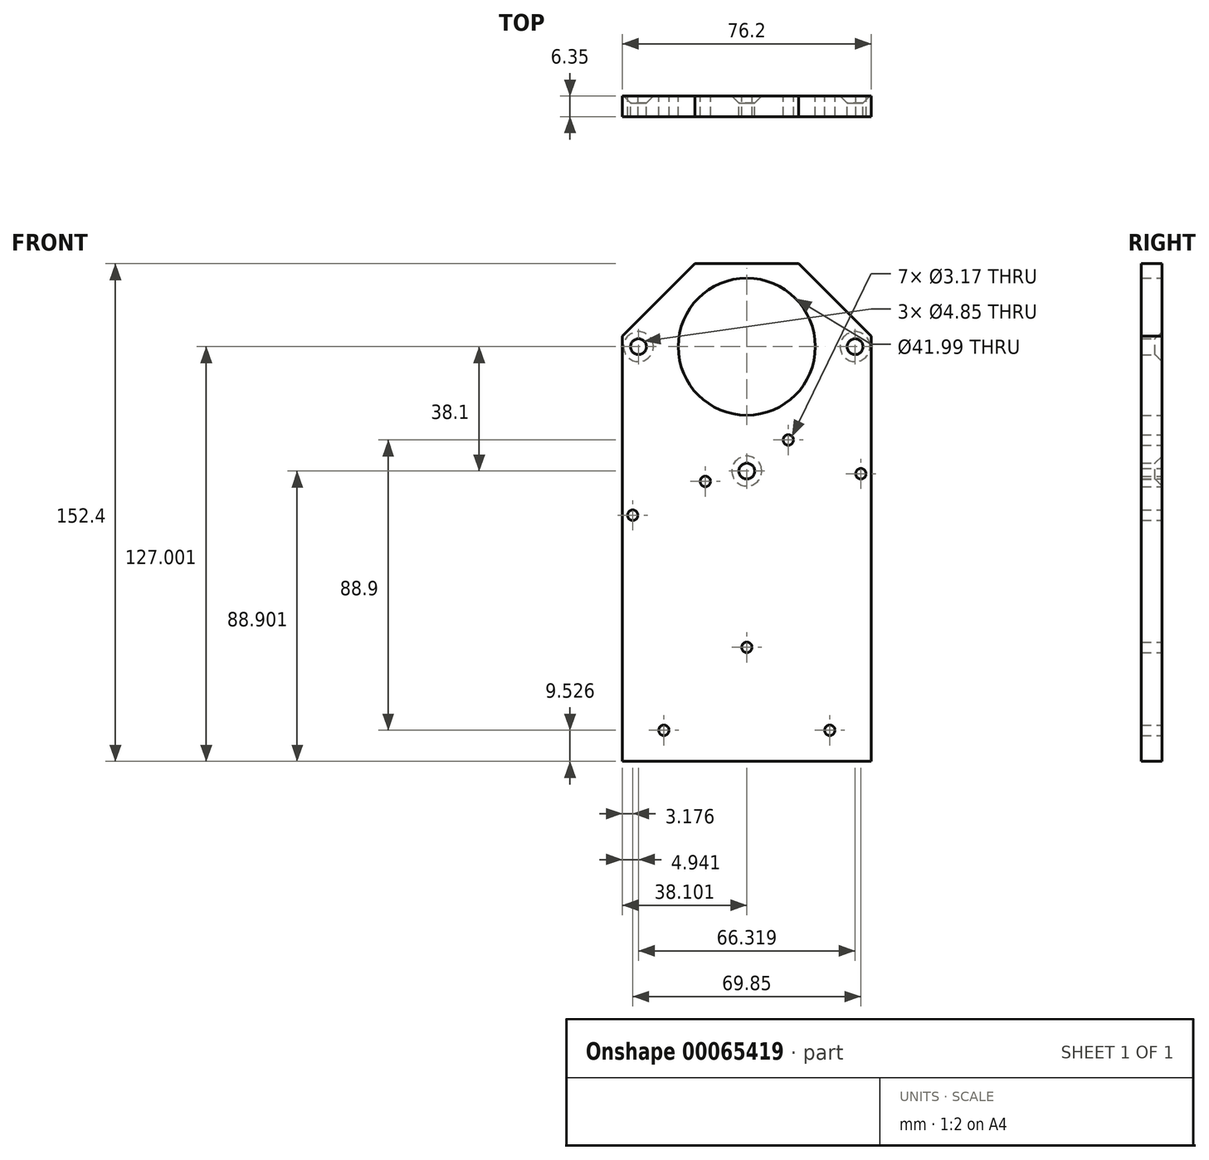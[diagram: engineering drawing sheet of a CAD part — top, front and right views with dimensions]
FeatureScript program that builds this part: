
annotation { "Feature Type Name" : "Feature", "Feature Type Description" : "" }
export const myFeature = defineFeature(function(context is Context, id is Id, definition is map)
    precondition{}
    {
        {
            var Q0;
            Q0=qCreatedBy(makeId("Front.planeOp"),FACE);
            var sketch = newSketch(context, id + "F0", { "sketchPlane" : qUnion([Q0])});
            skLineSegment(sketch, "E0", {"start": v(-20.16, 46.71) * mm, "end": v(11.59, 46.71) * mm});
            skLineSegment(sketch, "E1", {"start": v(11.59, 46.71) * mm, "end": v(33.81, 24.49) * mm});
            skLineSegment(sketch, "E2", {"start": v(-20.16, 46.71) * mm, "end": v(-42.39, 24.49) * mm});
            skLineSegment(sketch, "E3", {"start": v(-42.39, 24.49) * mm, "end": v(-42.39, -105.69) * mm});
            skLineSegment(sketch, "E4", {"start": v(33.81, 24.49) * mm, "end": v(33.81, -105.69) * mm});
            skLineSegment(sketch, "E5", {"start": v(33.81, -105.69) * mm, "end": v(-42.39, -105.69) * mm});
            skLineSegment(sketch, "E6", {"start": v(33.81, 24.49) * mm, "end": v(33.81, 21.31) * mm});
            skLineSegment(sketch, "E7", {"start": v(33.81, 21.31) * mm, "end": v(28.87, 21.31) * mm});
            skCircle(sketch, "E8", {"center": v(28.87, 21.31) * mm, "radius": 2.43 * mm});
            skLineSegment(sketch, "E9", {"start": v(-4.29, 46.71) * mm, "end": v(-4.29, -105.69) * mm});
            skLineSegment(sketch, "E10", {"start": v(33.81, 21.31) * mm, "end": v(33.81, -7.26) * mm});
            skLineSegment(sketch, "E11", {"start": v(33.81, -7.26) * mm, "end": v(8.41, -7.26) * mm});
            skLineSegment(sketch, "E12", {"start": v(33.81, -7.26) * mm, "end": v(33.81, -17.58) * mm});
            skLineSegment(sketch, "E13", {"start": v(33.81, -17.58) * mm, "end": v(30.64, -17.58) * mm});
            skLineSegment(sketch, "E14", {"start": v(-42.39, 24.49) * mm, "end": v(-42.39, -19.96) * mm});
            skLineSegment(sketch, "E15", {"start": v(-42.39, -19.96) * mm, "end": v(-16.99, -19.96) * mm});
            skLineSegment(sketch, "E16", {"start": v(-42.39, -19.96) * mm, "end": v(-42.39, -30.28) * mm});
            skLineSegment(sketch, "E17", {"start": v(-42.39, -30.28) * mm, "end": v(-39.21, -30.28) * mm});
            skCircle(sketch, "E18", {"center": v(-16.99, -19.96) * mm, "radius": 1.59 * mm});
            skCircle(sketch, "E19", {"center": v(-39.21, -30.28) * mm, "radius": 1.59 * mm});
            skCircle(sketch, "E20", {"center": v(8.41, -7.26) * mm, "radius": 1.59 * mm});
            skLineSegment(sketch, "E21", {"start": v(-16.99, -19.96) * mm, "end": v(-4.29, -19.96) * mm});
            skLineSegment(sketch, "E22", {"start": v(-4.29, -19.96) * mm, "end": v(-4.29, -16.79) * mm});
            skCircle(sketch, "E23", {"center": v(-4.29, -16.79) * mm, "radius": 2.43 * mm});
            skLineSegment(sketch, "E24", {"start": v(28.87, 21.31) * mm, "end": v(-4.29, 21.31) * mm});
            skCircle(sketch, "E25", {"center": v(-4.29, 21.31) * mm, "radius": 21 * mm});
            skLineSegment(sketch, "E26", {"start": v(-4.29, -105.69) * mm, "end": v(-4.29, -70.76) * mm});
            skLineSegment(sketch, "E27", {"start": v(-42.39, -105.69) * mm, "end": v(-29.69, -105.69) * mm});
            skLineSegment(sketch, "E28", {"start": v(33.81, -105.69) * mm, "end": v(21.11, -105.69) * mm});
            skLineSegment(sketch, "E29", {"start": v(21.11, -105.69) * mm, "end": v(21.11, -96.16) * mm});
            skLineSegment(sketch, "E30", {"start": v(-29.69, -105.69) * mm, "end": v(-29.69, -96.16) * mm});
            skCircle(sketch, "E31", {"center": v(-29.69, -96.16) * mm, "radius": 1.59 * mm});
            skCircle(sketch, "E32", {"center": v(21.11, -96.16) * mm, "radius": 1.59 * mm});
            skCircle(sketch, "E33", {"center": v(-4.29, -70.76) * mm, "radius": 1.59 * mm});
            skCircle(sketch, "E34.MirrorC", {"center": v(-37.45, 21.31) * mm, "radius": 2.43 * mm});
            skCircle(sketch, "E35", {"center": v(30.64, -17.58) * mm, "radius": 1.59 * mm});
            skSolve(sketch);
        }
        {
            var Q0;
            Q0 = qSketchRegion(id + "F0", true);
            extrude(context, id + "F1", {"entities" : qUnion([Q0]), "depth" : 6.35 * mm});
        }
        {
            var Q0;
            Q0=makeQuery(id+"F1.opExtrude","CAP_EDGE",EDGE,{"disambiguationData":[OSD([sQuery(id+"F0.wireOp",EDGE,"E8")])],"isStart":true});
            var Q1;
            Q1=makeQuery(id+"F1.opExtrude","CAP_EDGE",EDGE,{"disambiguationData":[OSD([sQuery(id+"F0.wireOp",EDGE,"E23")])],"isStart":true});
            var Q2;
            Q2=makeQuery(id+"F1.opExtrude","CAP_EDGE",EDGE,{"disambiguationData":[OSD([sQuery(id+"F0.wireOp",EDGE,"E34.MirrorC")])],"isStart":true});
            chamfer(context, id + "F2", {"entities" : qUnion([Q0, Q1, Q2]), "width" : 2.16 * mm, "tangentPropagation" : true});
        }
    });
